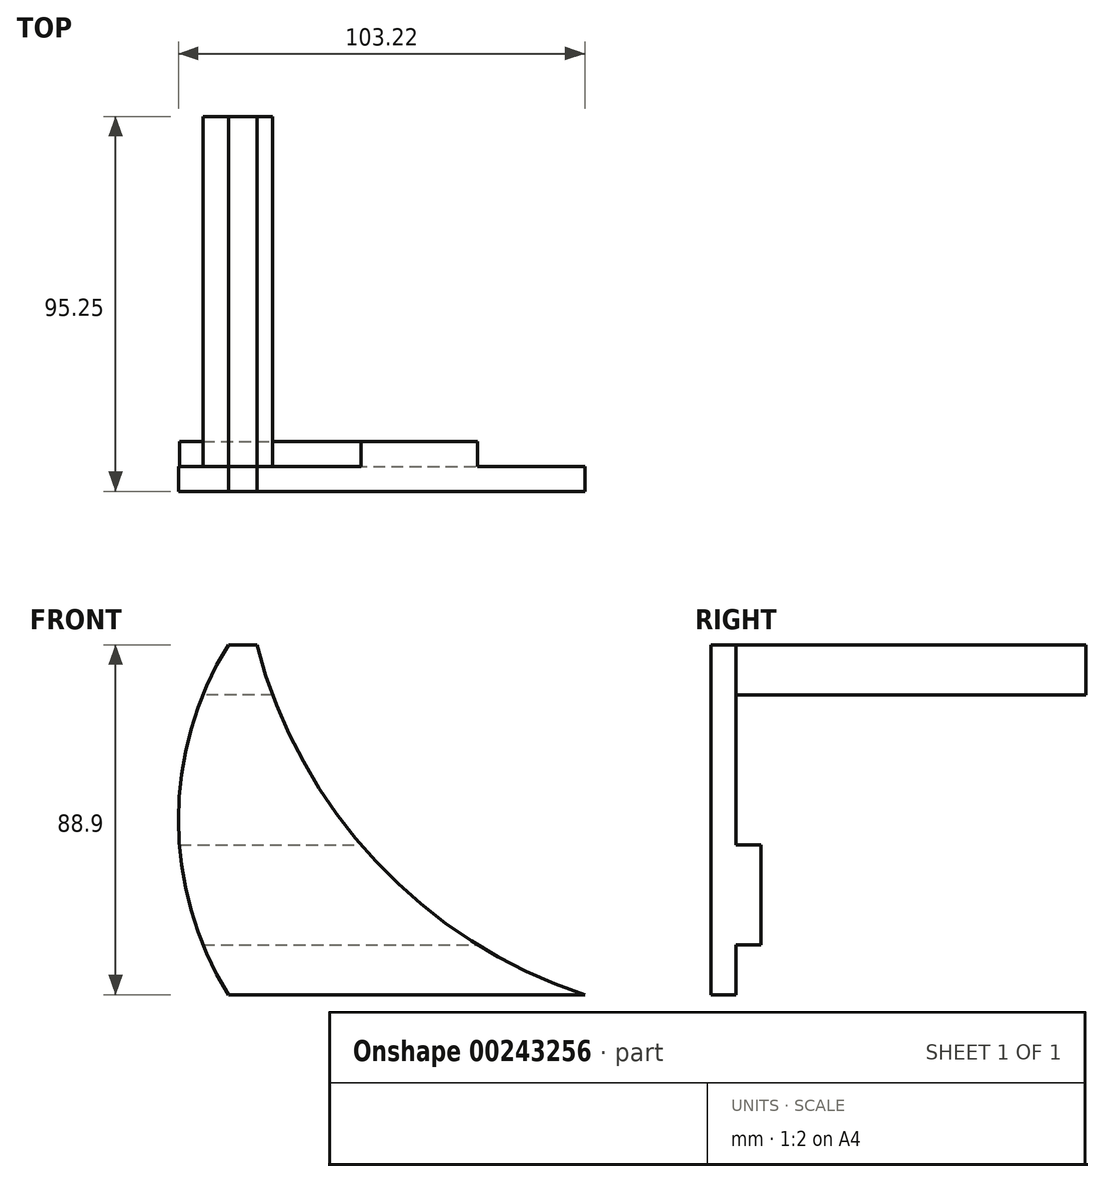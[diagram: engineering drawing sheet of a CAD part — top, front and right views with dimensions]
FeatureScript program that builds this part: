
annotation { "Feature Type Name" : "Feature", "Feature Type Description" : "" }
export const myFeature = defineFeature(function(context is Context, id is Id, definition is map)
    precondition{}
    {
        {
            var Q0;
            Q0=qCreatedBy(makeId("Front.planeOp"),FACE);
            var sketch = newSketch(context, id + "F0", { "sketchPlane" : qUnion([Q0])});
            skLineSegment(sketch, "E0", {"start": v(0, 0) * mm, "end": v(0, -88.9) * mm});
            skLineSegment(sketch, "E1", {"start": v(0, -88.9) * mm, "end": v(104.78, -88.9) * mm});
            skLineSegment(sketch, "E2", {"start": v(104.78, -88.9) * mm, "end": v(104.78, 0) * mm});
            skLineSegment(sketch, "E3", {"start": v(104.77, 0) * mm, "end": v(0, 0) * mm});
            skLineSegment(sketch, "E4", {"start": v(104.78, 0) * mm, "end": v(104.78, 31.75) * mm, "construction": true});
            skLineSegment(sketch, "E5", {"start": v(13.01, -88.9) * mm, "end": v(104.78, -88.9) * mm});
            skLineSegment(sketch, "E6", {"start": v(187.27, 31.75) * mm, "end": v(-39.47, 31.75) * mm, "construction": true});
            skLineSegment(sketch, "E7", {"start": v(142.88, 72.94) * mm, "end": v(142.88, -111.59) * mm, "construction": true});
            skCircle(sketch, "E8", {"center": v(142.88, 31.75) * mm, "radius": 127 * mm});
            skCircle(sketch, "E9", {"center": v(84.14, -44.45) * mm, "radius": 84.14 * mm});
            skLineSegment(sketch, "E10", {"start": v(6.22, -76.2) * mm, "end": v(75.97, -76.2) * mm});
            skLineSegment(sketch, "E11", {"start": v(0.24, -50.8) * mm, "end": v(46.36, -50.8) * mm});
            skPoint(sketch, "E12", {"position": v(12.7, 0) * mm});
            skPoint(sketch, "E13", {"position": v(19.9, 0) * mm});
            skSolve(sketch);
        }
        {
            var Q0;
            {var subQ0=sQuery(id+"F0.wireOp",EDGE,"E11");Q0=makeQuery(id+"F0.imprint","IMPRINT",FACE,{"disambiguationData":[TD([[makeQuery(id+"F0.imprint","IMPRINT",EDGE,{"derivedFrom":subQ0}),1.0]])]});}
            var Q1;
            {var subQ0=sQuery(id+"F0.wireOp",EDGE,"E10");Q1=makeQuery(id+"F0.imprint","IMPRINT",FACE,{"disambiguationData":[TD([[makeQuery(id+"F0.imprint","IMPRINT",EDGE,{"derivedFrom":subQ0}),1.0]])]});}
            var Q2;
            {var subQ0=sQuery(id+"F0.wireOp",EDGE,"E10");Q2=makeQuery(id+"F0.imprint","IMPRINT",FACE,{"disambiguationData":[TD([[makeQuery(id+"F0.imprint","IMPRINT",EDGE,{"derivedFrom":subQ0}),-1.0]])]});}
            extrude(context, id + "F1", {"entities" : qUnion([Q0, Q1, Q2]), "depth" : 6.35 * mm});
        }
        {
            var Q0;
            Q0=makeQuery(id+"F1.opExtrude","CAP_FACE",FACE,{"disambiguationData":[OSD([sQuery(id+"F0.wireOp",EDGE,"E1"),sQuery(id+"F0.wireOp",EDGE,"E3"),sQuery(id+"F0.wireOp",EDGE,"E5"),sQuery(id+"F0.wireOp",EDGE,"E8"),sQuery(id+"F0.wireOp",EDGE,"E9")])],"isStart":false});
            var sketch = newSketch(context, id + "F2", { "sketchPlane" : qUnion([Q0])});
            skLineSegment(sketch, "E14", {"start": v(6.22, -76.2) * mm, "end": v(75.97, -76.2) * mm});
            skLineSegment(sketch, "E15", {"start": v(0.24, -50.8) * mm, "end": v(46.36, -50.8) * mm});
            skLineSegment(sketch, "E16", {"start": v(29.46, -25.4) * mm, "end": v(2.18, -25.4) * mm});
            skSolve(sketch);
        }
        {
            var Q0;
            {var subQ0=sQuery(id+"F2.wireOp",EDGE,"E14");Q0=makeQuery(id+"F2.imprint","IMPRINT",FACE,{"disambiguationData":[TD([[makeQuery(id+"F2.imprint","IMPRINT",EDGE,{"derivedFrom":subQ0}),1.0]])]});}
            extrude(context, id + "F3", {"entities" : qUnion([Q0]), "operationType" : NewBodyOperationType.ADD, "oppositeDirection" : true, "depth" : 12.7 * mm});
        }
        {
            var Q0;
            {var subQ0=sQuery(id+"F0.wireOp",EDGE,"E9");var subQ1=sQuery(id+"F0.wireOp",EDGE,"E8");var subQ2=sQuery(id+"F0.wireOp",EDGE,"E3");Q0=makeQuery(id+"F3.boolean.opBoolean","SPLIT",FACE,{"disambiguationData":[TD([makeQuery(id+"F1.opExtrude","SWEPT_FACE",FACE,{"disambiguationData":[OSD([subQ2])]})])],"derivedFrom":makeQuery(id+"F1.opExtrude","CAP_FACE",FACE,{"disambiguationData":[OSD([sQuery(id+"F0.wireOp",EDGE,"E1"),subQ2,sQuery(id+"F0.wireOp",EDGE,"E5"),subQ1,subQ0])],"isStart":true})});}
            var sketch = newSketch(context, id + "F4", { "sketchPlane" : qUnion([Q0])});
            skLineSegment(sketch, "E17", {"start": v(-23.9, -12.7) * mm, "end": v(-6.22, -12.7) * mm});
            skSolve(sketch);
        }
        {
            var Q0;
            {var subQ0=sQuery(id+"F4.wireOp",EDGE,"E17");Q0=makeQuery(id+"F4.imprint","IMPRINT",FACE,{"disambiguationData":[TD([[makeQuery(id+"F4.imprint","IMPRINT",EDGE,{"derivedFrom":subQ0}),1.0]])]});}
            extrude(context, id + "F5", {"entities" : qUnion([Q0]), "depth" : 88.9 * mm});
        }
    });
